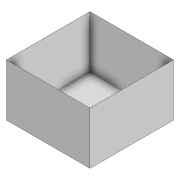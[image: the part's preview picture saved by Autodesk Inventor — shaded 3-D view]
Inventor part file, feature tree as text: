
AUTODESK INVENTOR PART (.ipt)
format: ipt  version: 2022 (Build 260153000, 153)  size: 80,384 bytes
history: native  units: mm
features: extrude x1, delete_face x1, sketch x1
ambient origin geometry x8: Origin, YZ Plane, XZ Plane, XY Plane, X Axis, Y Axis, Z Axis, Center Point
bodies: Solid1 (feature_tree)
feature tree (3):
  extrude  "Extrusion1"  Depth=80.0mm
  delete_face  "Delete Face1"
  sketch  "Sketch1"  dims[d0=80.0mm d1=50.0mm d2=80.0mm d3=0.0mm]
